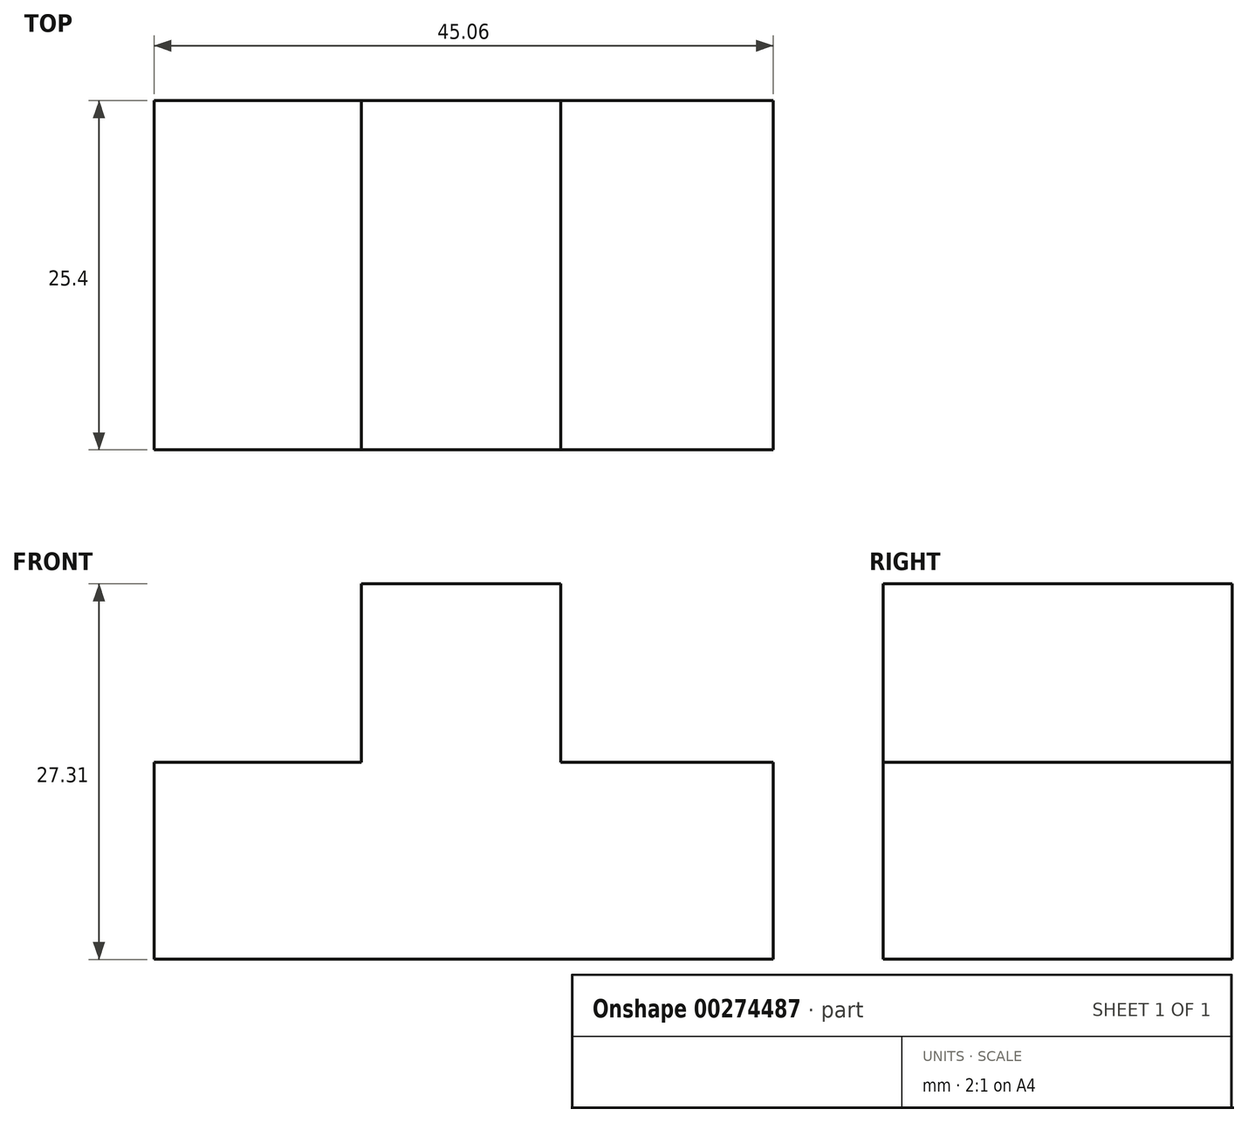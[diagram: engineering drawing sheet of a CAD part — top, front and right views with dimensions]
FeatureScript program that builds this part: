
annotation { "Feature Type Name" : "Feature", "Feature Type Description" : "" }
export const myFeature = defineFeature(function(context is Context, id is Id, definition is map)
    precondition{}
    {
        {
            var Q0;
            Q0=qCreatedBy(makeId("Front.planeOp"),FACE);
            var sketch = newSketch(context, id + "F0", { "sketchPlane" : qUnion([Q0])});
            skLineSegment(sketch, "E0", {"start": v(-62.25, 19.29) * mm, "end": v(-62.25, 4.96) * mm});
            skLineSegment(sketch, "E1", {"start": v(-62.25, 4.96) * mm, "end": v(-17.19, 4.96) * mm});
            skLineSegment(sketch, "E2", {"start": v(-17.19, 4.96) * mm, "end": v(-17.19, 19.29) * mm});
            skLineSegment(sketch, "E3", {"start": v(-17.19, 19.29) * mm, "end": v(-32.65, 19.29) * mm});
            skLineSegment(sketch, "E4", {"start": v(-32.65, 19.29) * mm, "end": v(-32.65, 32.27) * mm});
            skLineSegment(sketch, "E5", {"start": v(-32.65, 32.27) * mm, "end": v(-47.17, 32.27) * mm});
            skLineSegment(sketch, "E6", {"start": v(-47.17, 32.27) * mm, "end": v(-47.17, 19.29) * mm});
            skLineSegment(sketch, "E7", {"start": v(-47.17, 19.29) * mm, "end": v(-62.25, 19.29) * mm});
            skSolve(sketch);
        }
        {
            var Q0;
            Q0 = qSketchRegion(id + "F0", true);
            extrude(context, id + "F1", {"entities" : qUnion([Q0]), "depth" : 25.4 * mm});
        }
    });
